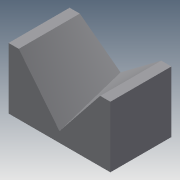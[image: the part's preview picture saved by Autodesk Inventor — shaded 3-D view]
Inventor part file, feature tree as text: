
AUTODESK INVENTOR PART (.ipt)
format: ipt  version: 2015 (Build 190159000, 159)  size: 114,176 bytes
history: native  units: in
note: dims shown in document units (in); Inventor stores cm internally (conversion verified against a paired STEP export)
features: sketch x3, projected_geometry x2, extrude x1, loft x1
ambient origin geometry x8: Origin, YZ Plane, XZ Plane, XY Plane, X Axis, Y Axis, Z Axis, Center Point
bodies: Solid1 (feature_tree)
feature tree (7):
  extrude  "Extrusion1"  Depth=1.5in
  loft  "Loft1"
  sketch  "Sketch1"  dims[d0=2.5in d1=1.5in]
  sketch  "Sketch2"  dims[d2=1.5in d3=0.0in d4=0.25in]
  projected_geometry  "Projected Loop1"
  sketch  "Sketch3"  dims[d5=0.25in d6=0.25in d7=0.75in d8=0.25in d9=0.25in d10=0.0in d11=90.0deg d12=0.0in d13=90.0deg]
  projected_geometry  "Projected Loop2"
